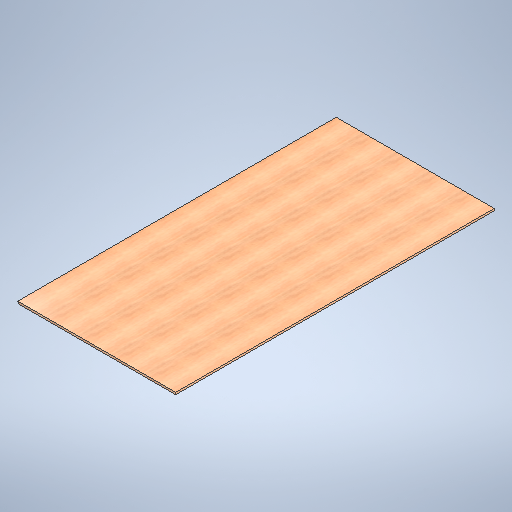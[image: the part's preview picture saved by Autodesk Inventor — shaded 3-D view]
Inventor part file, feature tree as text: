
AUTODESK INVENTOR PART (.ipt)
format: ipt  version: 2025.1 (Build 291241020, 241B)  size: 321,024 bytes
history: native  units: in
note: dims shown in document units (in); Inventor stores cm internally (conversion verified against a paired STEP export)
features: extrude x1, sketch x1
ambient origin geometry x8: Origin, YZ Plane, XZ Plane, XY Plane, X Axis, Y Axis, Z Axis, Center Point
bodies: Body1 (feature_tree)
feature tree (2):
  extrude  "Extrusion2"  Depth=47.396in
  sketch  "Sketch2"  dims[d8=0.625in d9=0.1251in d11=96.0in d12=0.0in d14=47.396in]
